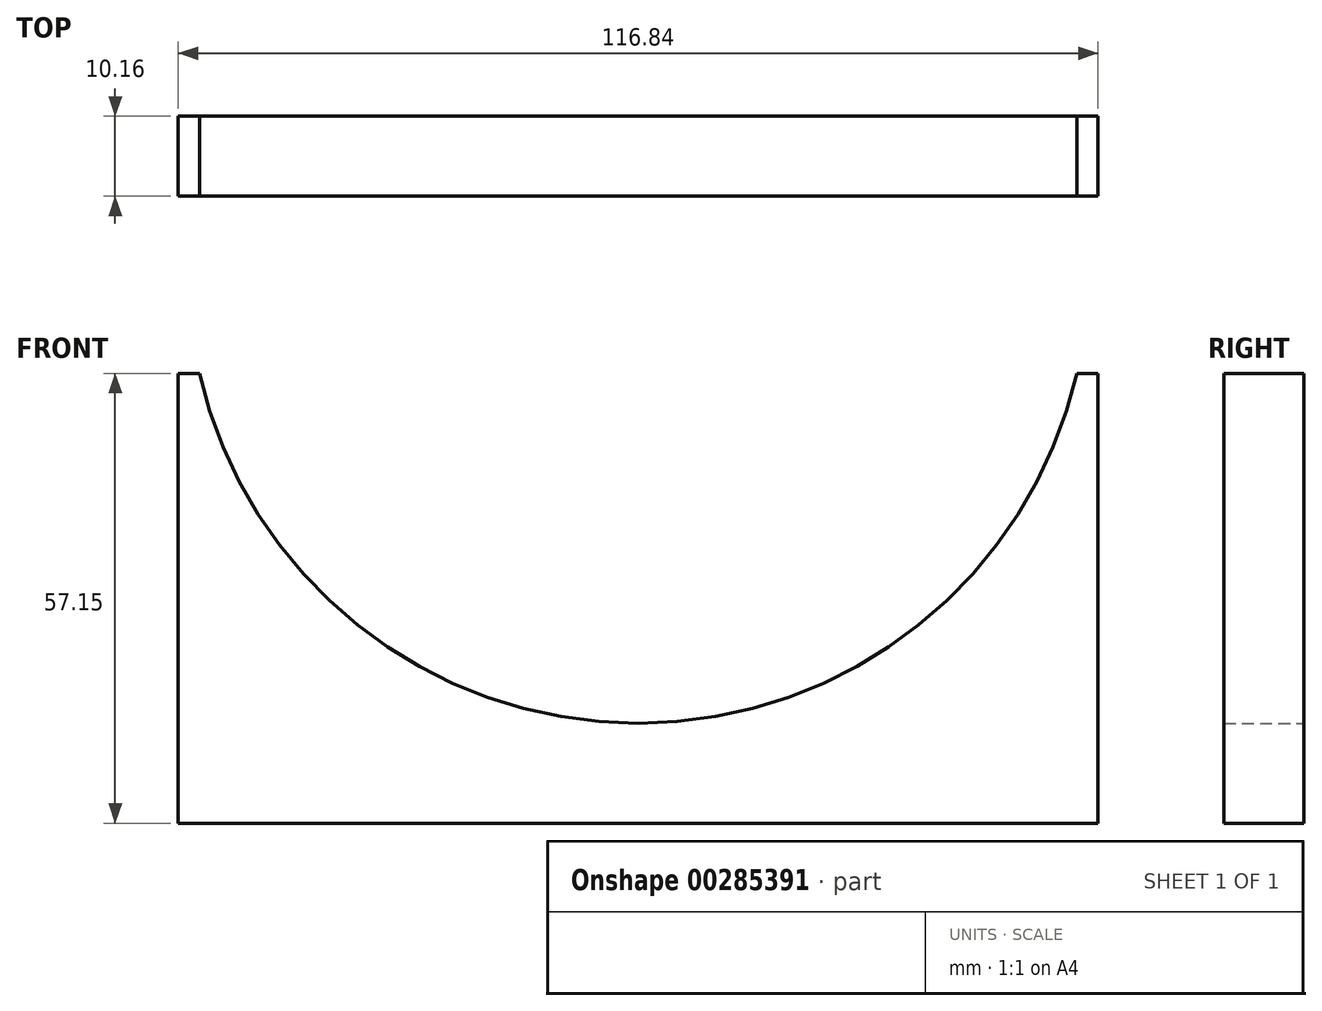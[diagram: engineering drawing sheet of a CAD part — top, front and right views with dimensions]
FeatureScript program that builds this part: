
annotation { "Feature Type Name" : "Feature", "Feature Type Description" : "" }
export const myFeature = defineFeature(function(context is Context, id is Id, definition is map)
    precondition{}
    {
        {
            var Q0;
            Q0=qCreatedBy(makeId("Front.planeOp"),FACE);
            var sketch = newSketch(context, id + "F0", { "sketchPlane" : qUnion([Q0])});
            skLineSegment(sketch, "E0.bottom", {"start": v(0, 0) * mm, "end": v(-116.84, 0) * mm});
            skLineSegment(sketch, "E0.top", {"start": v(0, 57.15) * mm, "end": v(-2.7, 57.15) * mm});
            skLineSegment(sketch, "E0.left", {"start": v(0, 0) * mm, "end": v(0, 57.15) * mm});
            skLineSegment(sketch, "E0.right", {"start": v(-116.84, 0) * mm, "end": v(-116.84, 57.15) * mm});
            skPoint(sketch, "E1.endSnap0", {"position": v(-58.42, 57.15) * mm});
            skPoint(sketch, "E2.endSnap0", {"position": v(-58.42, 6.35) * mm});
            skArc(sketch, "E3", {"start": v(-114.14, 57.15) * mm, "mid": v(-58.42, 12.7) * mm, "end": v(-2.7, 57.15) * mm});
            skLineSegment(sketch, "E4.trimOffspring", {"start": v(-114.14, 57.15) * mm, "end": v(-116.84, 57.15) * mm});
            skSolve(sketch);
        }
        {
            var Q0;
            Q0=makeQuery(id+"F0.imprint","IMPRINT",FACE,{"disambiguationData":[TD([[makeQuery(id+"F0.imprint","IMPRINT",EDGE,{"derivedFrom":sQuery(id+"F0.wireOp",EDGE,"E0.bottom")}),-1.0]])]});
            extrude(context, id + "F1", {"entities" : qUnion([Q0]), "depth" : 10.16 * mm});
        }
    });
